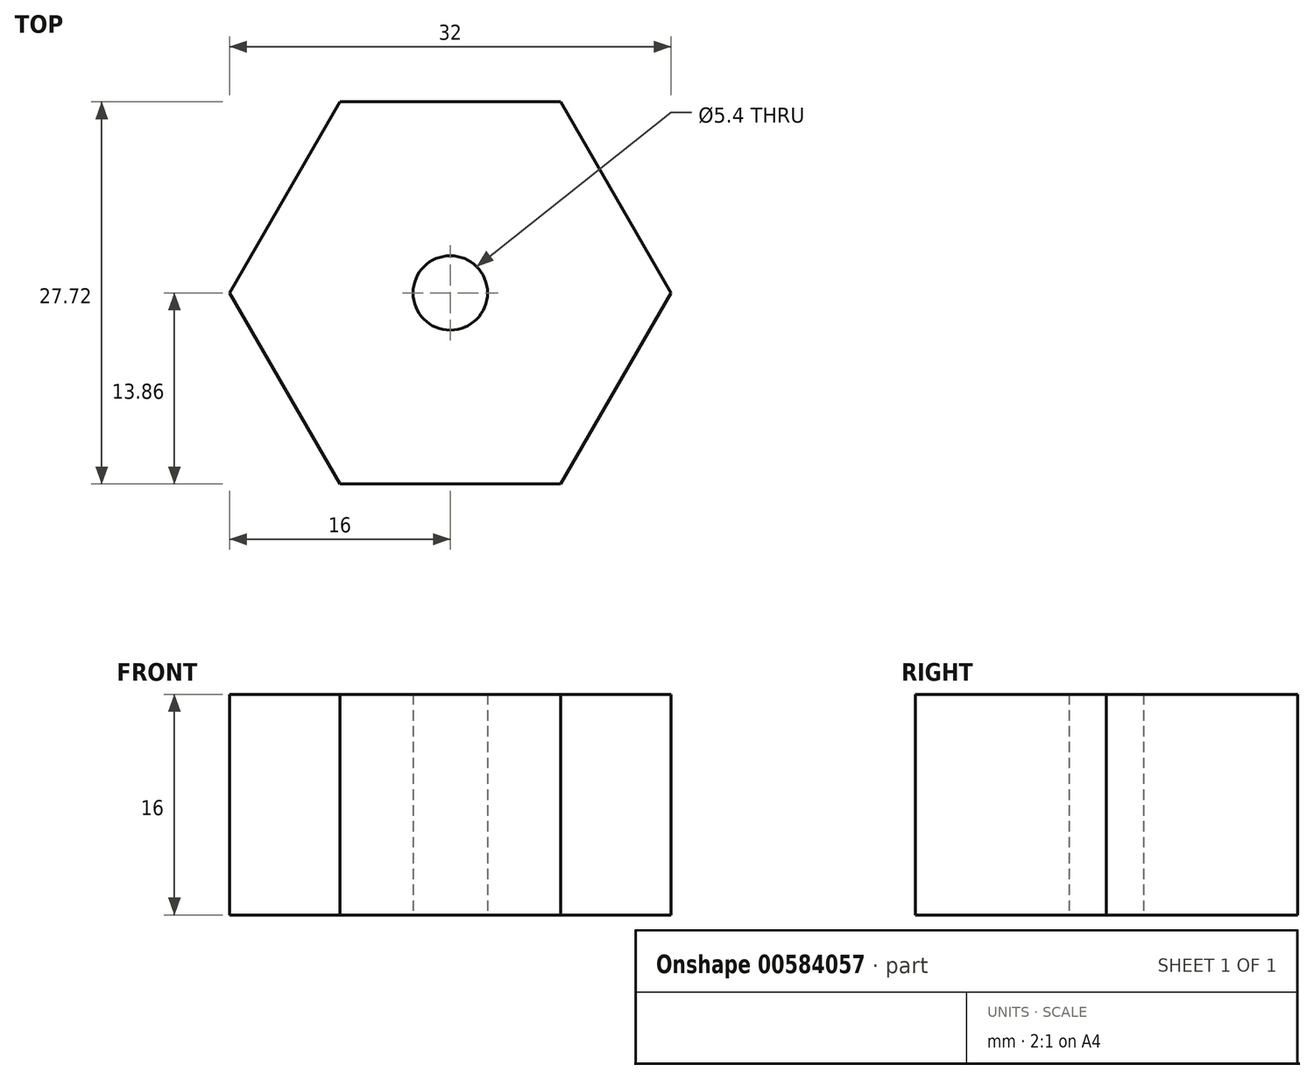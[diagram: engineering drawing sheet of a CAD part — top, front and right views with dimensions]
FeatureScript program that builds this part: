
annotation { "Feature Type Name" : "Feature", "Feature Type Description" : "" }
export const myFeature = defineFeature(function(context is Context, id is Id, definition is map)
    precondition{}
    {
        {
            var Q0;
            Q0=qCreatedBy(makeId("Top.planeOp"),FACE);
            var sketch = newSketch(context, id + "F0", { "sketchPlane" : qUnion([Q0])});
            skCircle(sketch, "E0.cCircle", {"center": v(0, 0) * mm, "radius": 16 * mm, "construction": true});
            skLineSegment(sketch, "E0.0", {"start": v(16, 0) * mm, "end": v(8, -13.86) * mm});
            skLineSegment(sketch, "E0.1", {"start": v(8, -13.86) * mm, "end": v(-8, -13.86) * mm});
            skLineSegment(sketch, "E0.2", {"start": v(-8, -13.86) * mm, "end": v(-16, 0) * mm});
            skLineSegment(sketch, "E0.3", {"start": v(-16, 0) * mm, "end": v(-8, 13.86) * mm});
            skLineSegment(sketch, "E0.4", {"start": v(-8, 13.86) * mm, "end": v(8, 13.86) * mm});
            skLineSegment(sketch, "E0.5", {"start": v(8, 13.86) * mm, "end": v(16, 0) * mm});
            skCircle(sketch, "E1", {"center": v(0, 0) * mm, "radius": 2.7 * mm});
            skSolve(sketch);
        }
        {
            var Q0;
            Q0 = qSketchRegion(id + "F0", true);
            extrude(context, id + "F1", {"entities" : qUnion([Q0]), "depth" : 16 * mm, "offsetDistance" : 25 * mm});
        }
    });
